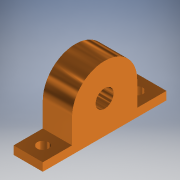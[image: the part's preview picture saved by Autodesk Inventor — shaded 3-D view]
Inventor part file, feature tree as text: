
AUTODESK INVENTOR PART (.ipt)
format: ipt  version: 2019 (Build 230136000, 136)  size: 123,392 bytes
history: native  units: in
note: dims shown in document units (in); Inventor stores cm internally (conversion verified against a paired STEP export)
features: extrude x2, sketch x2
ambient origin geometry x8: Origin, YZ Plane, XZ Plane, XY Plane, X Axis, Y Axis, Z Axis, Center Point
bodies: Solid1 (feature_tree)
feature tree (4):
  extrude  "Extrusion1"  Depth=2.1654in
  extrude  "Extrusion2"  Depth=0.5118in
  sketch  "Sketch1"  dims[d0=2.1654in d2=0.315in]
  sketch  "Sketch2"  dims[d3=0.5118in d4=0.0in d5=0.1969in d6=0.1969in d7=0.5118in d8=0.0in]
